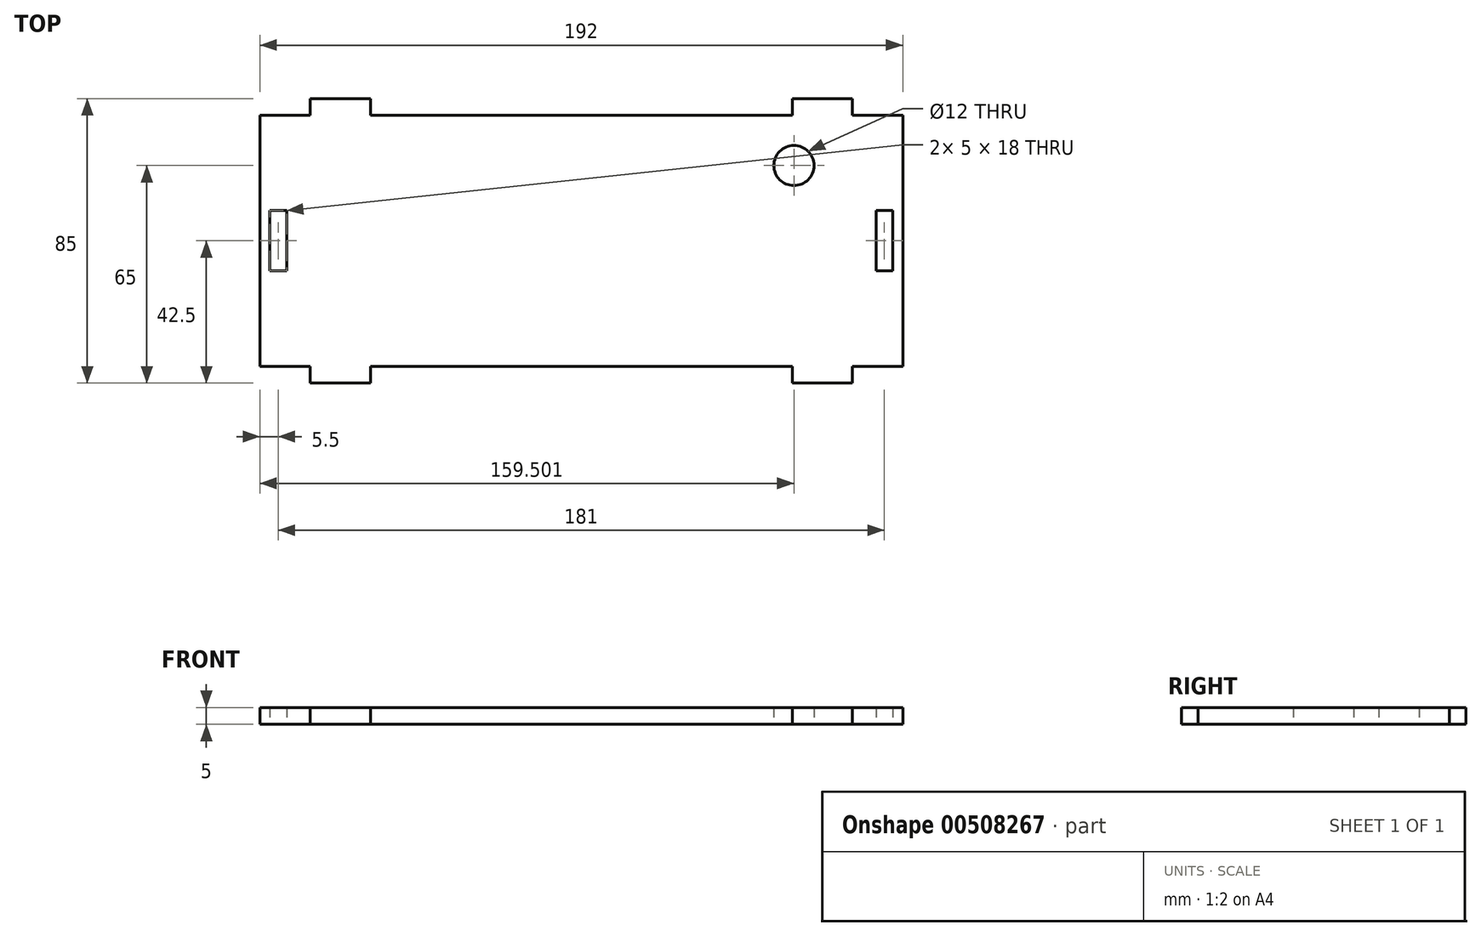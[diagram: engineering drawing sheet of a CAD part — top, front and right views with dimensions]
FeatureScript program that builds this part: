
annotation { "Feature Type Name" : "Feature", "Feature Type Description" : "" }
export const myFeature = defineFeature(function(context is Context, id is Id, definition is map)
    precondition{}
    {
        {
            var Q0;
            Q0=qCreatedBy(makeId("Top.planeOp"),FACE);
            var sketch = newSketch(context, id + "F0", { "sketchPlane" : qUnion([Q0])});
            skLineSegment(sketch, "E0.bottom", {"start": v(96, 37.5) * mm, "end": v(81, 37.5) * mm});
            skLineSegment(sketch, "E0.top", {"start": v(96, -37.5) * mm, "end": v(81, -37.5) * mm});
            skPoint(sketch, "E0.middle", {"position": v(0, 0) * mm});
            skLineSegment(sketch, "E1.top", {"start": v(63, -42.5) * mm, "end": v(81, -42.5) * mm});
            skLineSegment(sketch, "E1.left", {"start": v(63, -37.5) * mm, "end": v(63, -42.5) * mm});
            skLineSegment(sketch, "E1.right", {"start": v(81, -37.5) * mm, "end": v(81, -42.5) * mm});
            skLineSegment(sketch, "E2.top", {"start": v(-81, -42.5) * mm, "end": v(-63, -42.5) * mm});
            skLineSegment(sketch, "E2.left", {"start": v(-81, -37.5) * mm, "end": v(-81, -42.5) * mm});
            skLineSegment(sketch, "E2.right", {"start": v(-63, -37.5) * mm, "end": v(-63, -42.5) * mm});
            skLineSegment(sketch, "E3.trimOffspring", {"start": v(-81, 37.5) * mm, "end": v(-96, 37.5) * mm});
            skLineSegment(sketch, "E4.trimOffspring", {"start": v(63, 37.5) * mm, "end": v(-63, 37.5) * mm});
            skLineSegment(sketch, "E5.trimOffspring", {"start": v(63, -37.5) * mm, "end": v(-63, -37.5) * mm});
            skLineSegment(sketch, "E6.trimOffspring", {"start": v(-81, -37.5) * mm, "end": v(-96, -37.5) * mm});
            skLineSegment(sketch, "E7", {"start": v(0, 0) * mm, "end": v(0, 8.47) * mm, "construction": true});
            skLineSegment(sketch, "E8", {"start": v(0, 0) * mm, "end": v(7.23, 0) * mm, "construction": true});
            skLineSegment(sketch, "E9", {"start": v(-96, 37.5) * mm, "end": v(-96, -37.5) * mm});
            skLineSegment(sketch, "E10", {"start": v(96, 37.5) * mm, "end": v(96, -37.5) * mm});
            skLineSegment(sketch, "E11.bottom", {"start": v(-93, 9) * mm, "end": v(-88, 9) * mm});
            skLineSegment(sketch, "E11.top", {"start": v(-93, -9) * mm, "end": v(-88, -9) * mm});
            skLineSegment(sketch, "E11.left", {"start": v(-93, 9) * mm, "end": v(-93, -9) * mm});
            skLineSegment(sketch, "E11.right", {"start": v(-88, 9) * mm, "end": v(-88, -9) * mm});
            skLineSegment(sketch, "E12.bottom", {"start": v(88, 9) * mm, "end": v(93, 9) * mm});
            skLineSegment(sketch, "E12.top", {"start": v(88, -9) * mm, "end": v(93, -9) * mm});
            skLineSegment(sketch, "E12.left", {"start": v(88, 9) * mm, "end": v(88, -9) * mm});
            skLineSegment(sketch, "E12.right", {"start": v(93, 9) * mm, "end": v(93, -9) * mm});
            skCircle(sketch, "E13", {"center": v(63.5, 22.5) * mm, "radius": 6 * mm});
            skLineSegment(sketch, "E14", {"start": v(-81, 37.5) * mm, "end": v(-81, 42.5) * mm});
            skLineSegment(sketch, "E15", {"start": v(-81, 42.5) * mm, "end": v(-63, 42.5) * mm});
            skLineSegment(sketch, "E16", {"start": v(-63, 42.5) * mm, "end": v(-63, 37.5) * mm});
            skLineSegment(sketch, "E17.MirrorCS", {"start": v(63, 42.5) * mm, "end": v(63, 37.5) * mm});
            skLineSegment(sketch, "E18.MirrorCS", {"start": v(81, 42.5) * mm, "end": v(63, 42.5) * mm});
            skLineSegment(sketch, "E19.MirrorCS", {"start": v(81, 37.5) * mm, "end": v(81, 42.5) * mm});
            skSolve(sketch);
        }
        {
            var Q0;
            Q0=makeQuery(id+"F0.imprint","IMPRINT",FACE,{"disambiguationData":[TD([[makeQuery(id+"F0.imprint","IMPRINT",EDGE,{"derivedFrom":sQuery(id+"F0.wireOp",EDGE,"E0.bottom")}),1.0]])]});
            extrude(context, id + "F1", {"entities" : qUnion([Q0]), "depth" : 5 * mm});
        }
    });
